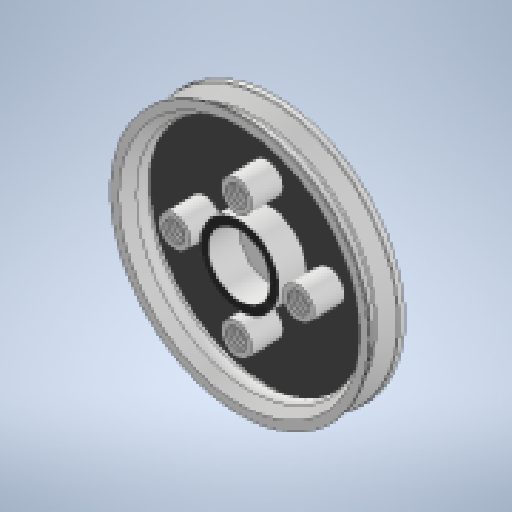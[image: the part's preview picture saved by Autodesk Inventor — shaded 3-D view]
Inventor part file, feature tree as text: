
AUTODESK INVENTOR PART (.ipt)
format: ipt  version: 2024.2 (Build 282272000, 272)  size: 238,080 bytes
history: native  units: mm
features: extrude x3, sketch x3, revolve x1, shell x1, projected_geometry x1
ambient origin geometry x8: Origin, YZ Plane, XZ Plane, XY Plane, X Axis, Y Axis, Z Axis, Center Point
bodies: Body1 (feature_tree)
feature tree (9):
  revolve  "Вращение2"
  shell  "Оболочка1"  Thickness=3.1mm
  extrude  "Выдавливание1"  Depth=0.2mm
  sketch  "Эскиз3"
  extrude  "Выдавливание2"  Depth=0.2mm
  extrude  "Выдавливание3"  Depth=1.55mm
  sketch  "Эскиз1"
  sketch  "Эскиз2"
  projected_geometry  "Спроецированная петля1"
